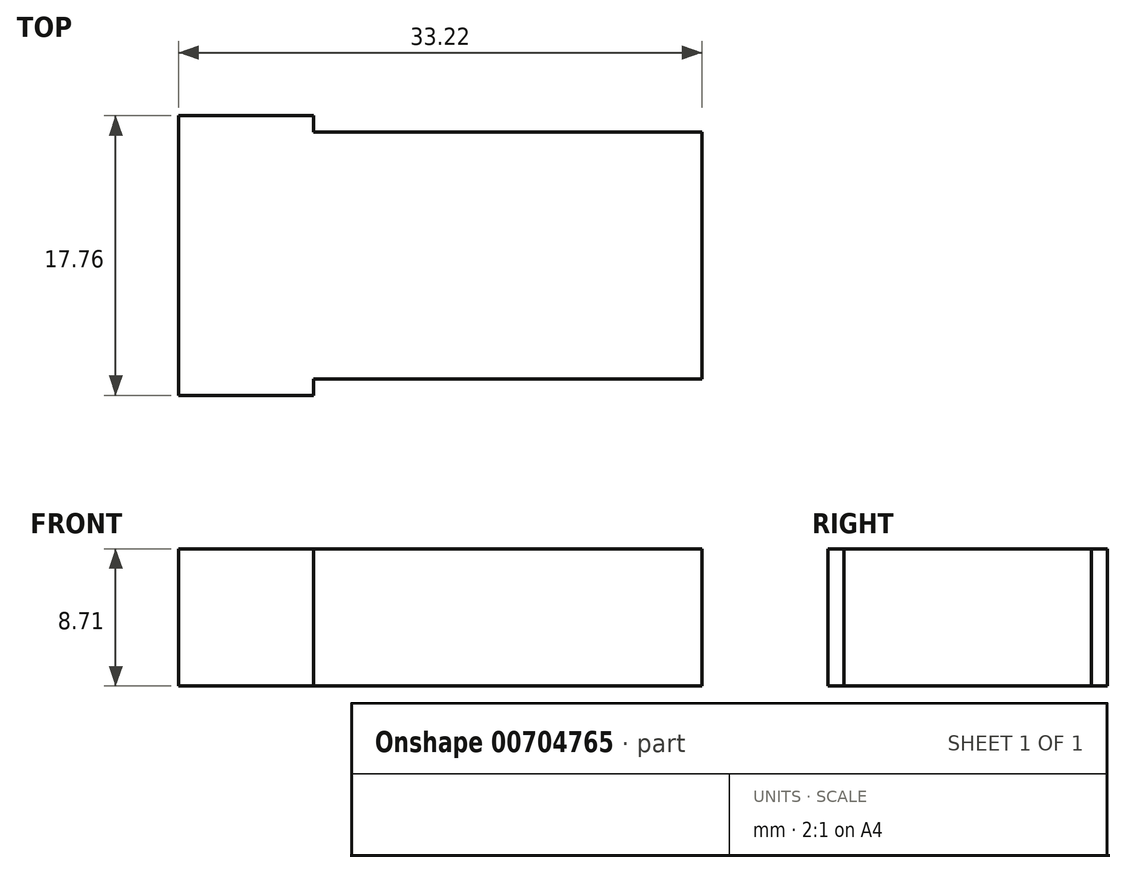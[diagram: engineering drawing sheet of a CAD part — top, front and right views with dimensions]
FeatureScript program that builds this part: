
annotation { "Feature Type Name" : "Feature", "Feature Type Description" : "" }
export const myFeature = defineFeature(function(context is Context, id is Id, definition is map)
    precondition{}
    {
        {
            var Q0;
            Q0=qCreatedBy(makeId("Front.planeOp"),FACE);
            var sketch = newSketch(context, id + "F0", { "sketchPlane" : qUnion([Q0])});
            skLineSegment(sketch, "E0.bottom", {"start": v(0, 0) * mm, "end": v(33.22, 0) * mm});
            skLineSegment(sketch, "E0.top", {"start": v(0, 8.7) * mm, "end": v(33.22, 8.7) * mm});
            skLineSegment(sketch, "E0.left", {"start": v(0, 0) * mm, "end": v(0, 8.7) * mm});
            skLineSegment(sketch, "E0.right", {"start": v(33.22, 0) * mm, "end": v(33.22, 8.7) * mm});
            skSolve(sketch);
        }
        {
            var Q0;
            Q0=makeQuery(id+"F0.imprint","IMPRINT",FACE,{"disambiguationData":[TD([[makeQuery(id+"F0.imprint","IMPRINT",EDGE,{"derivedFrom":sQuery(id+"F0.wireOp",EDGE,"E0.bottom")}),1.0]])]});
            extrude(context, id + "F1", {"entities" : qUnion([Q0]), "depth" : 17.76 * mm, "offsetDistance" : 25 * mm});
        }
        {
            var Q0;
            Q0=makeQuery(id+"F1.opExtrude","SWEPT_FACE",FACE,{"disambiguationData":[OSD([sQuery(id+"F0.wireOp",EDGE,"E0.right")])]});
            var sketch = newSketch(context, id + "F2", { "sketchPlane" : qUnion([Q0])});
            skLineSegment(sketch, "E1.bottom", {"start": v(-17.76, 8.7) * mm, "end": v(-16.73, 8.7) * mm});
            skLineSegment(sketch, "E1.top", {"start": v(-17.76, 0) * mm, "end": v(-16.73, 0) * mm});
            skLineSegment(sketch, "E1.left", {"start": v(-17.76, 8.7) * mm, "end": v(-17.76, 0) * mm});
            skLineSegment(sketch, "E1.right", {"start": v(-16.73, 8.7) * mm, "end": v(-16.73, 0) * mm});
            skLineSegment(sketch, "E2.bottom", {"start": v(-1.03, 8.7) * mm, "end": v(0, 8.7) * mm});
            skLineSegment(sketch, "E2.top", {"start": v(-1.03, 0) * mm, "end": v(0, 0) * mm});
            skLineSegment(sketch, "E2.left", {"start": v(-1.03, 8.7) * mm, "end": v(-1.03, 0) * mm});
            skLineSegment(sketch, "E2.right", {"start": v(0, 8.7) * mm, "end": v(0, 0) * mm});
            skSolve(sketch);
        }
        {
            var Q0;
            Q0=makeQuery(id+"F2.imprint","IMPRINT",FACE,{"disambiguationData":[TD([[makeQuery(id+"F2.imprint","IMPRINT",EDGE,{"derivedFrom":sQuery(id+"F2.wireOp",EDGE,"E1.bottom")}),-1.0]])]});
            var Q1;
            Q1=makeQuery(id+"F2.imprint","IMPRINT",FACE,{"disambiguationData":[TD([[makeQuery(id+"F2.imprint","IMPRINT",EDGE,{"derivedFrom":sQuery(id+"F2.wireOp",EDGE,"E2.bottom")}),-1.0]])]});
            extrude(context, id + "F3", {"entities" : qUnion([Q0, Q1]), "operationType" : NewBodyOperationType.REMOVE, "oppositeDirection" : true, "depth" : 24.65 * mm, "offsetDistance" : 25 * mm});
        }
    });
